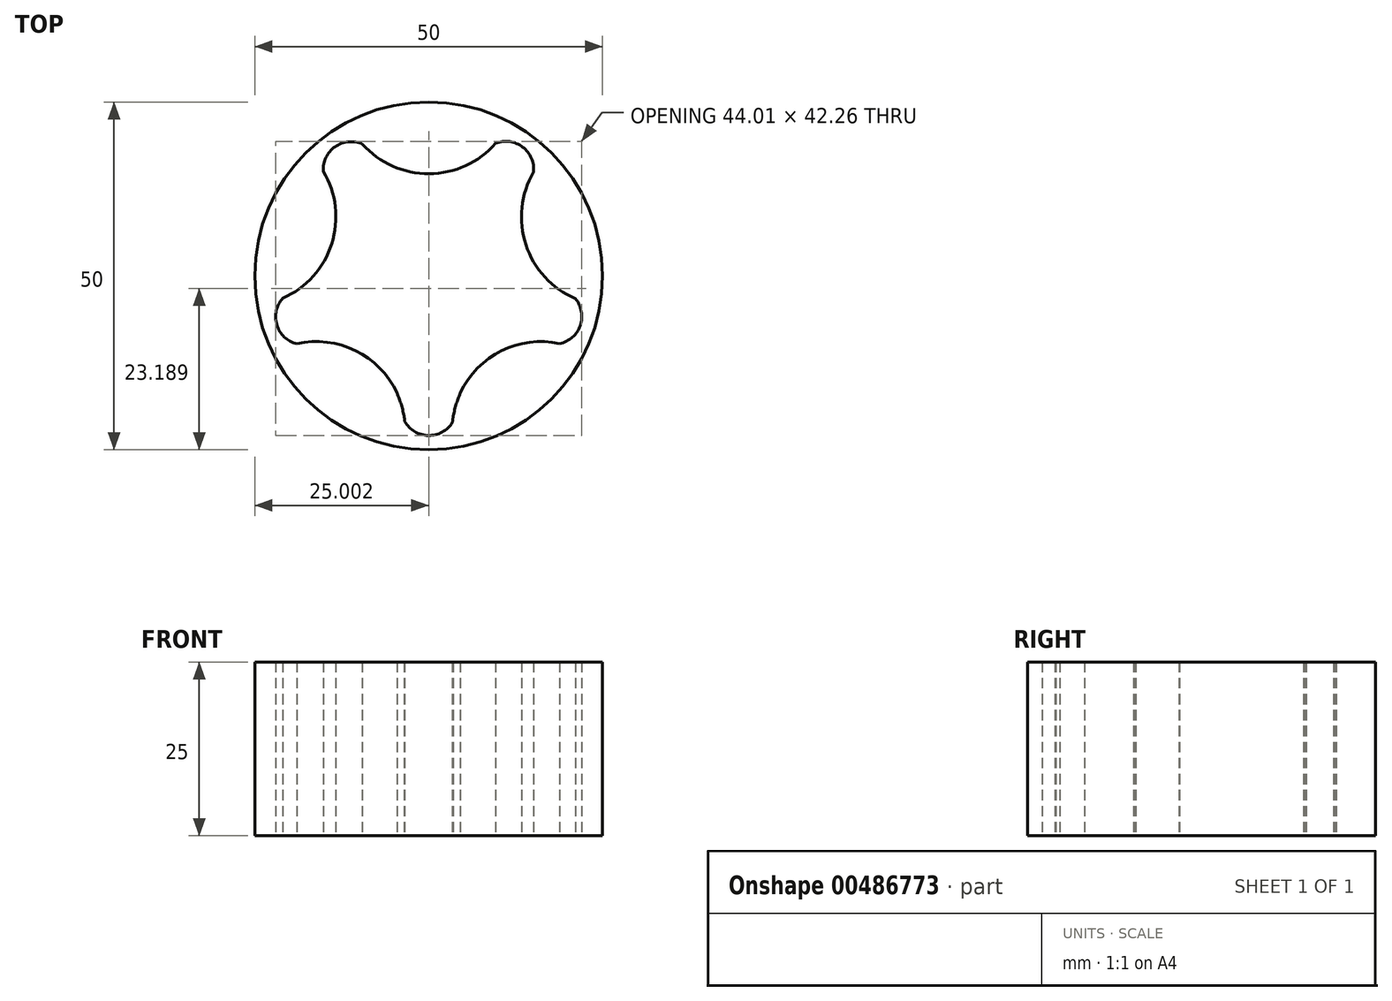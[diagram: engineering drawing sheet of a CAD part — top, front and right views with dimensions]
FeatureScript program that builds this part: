
annotation { "Feature Type Name" : "Feature", "Feature Type Description" : "" }
export const myFeature = defineFeature(function(context is Context, id is Id, definition is map)
    precondition{}
    {
        {
            var Q0;
            Q0=qCreatedBy(makeId("Top.planeOp"),FACE);
            var sketch = newSketch(context, id + "F0", { "sketchPlane" : qUnion([Q0])});
            skPoint(sketch, "E0", {"position": v(-17.88, 27.25) * mm});
            skPoint(sketch, "E1", {"position": v(-1.38, 10.75) * mm});
            skArc(sketch, "E2", {"start": v(-14.38, 27.25) * mm, "mid": v(-9.94, 18.7) * mm, "end": v(-1.38, 14.25) * mm});
            skArc(sketch, "E3.MirrorCS", {"start": v(-14.38, -5.75) * mm, "mid": v(-9.94, 2.8) * mm, "end": v(-1.38, 7.25) * mm});
            skArc(sketch, "E4.MirrorCS", {"start": v(-21.38, 27.25) * mm, "mid": v(-25.83, 18.7) * mm, "end": v(-34.38, 14.25) * mm});
            skArc(sketch, "E5.MirrorCS", {"start": v(-21.38, -5.75) * mm, "mid": v(-25.83, 2.8) * mm, "end": v(-34.38, 7.25) * mm});
            skArc(sketch, "E6", {"start": v(-14.38, 27.25) * mm, "mid": v(-17.88, 29.32) * mm, "end": v(-21.38, 27.25) * mm});
            skArc(sketch, "E7.MirrorCS", {"start": v(-14.38, -5.75) * mm, "mid": v(-17.88, -7.81) * mm, "end": v(-21.38, -5.75) * mm});
            skArc(sketch, "E8", {"start": v(-1.38, 7.25) * mm, "mid": v(0.68, 10.75) * mm, "end": v(-1.38, 14.25) * mm});
            skArc(sketch, "E9.MirrorCS", {"start": v(-34.38, 7.25) * mm, "mid": v(-36.45, 10.75) * mm, "end": v(-34.38, 14.25) * mm});
            skArc(sketch, "E10", {"start": v(-27.41, 33.59) * mm, "mid": v(-17.82, 29.32) * mm, "end": v(-8.26, 33.7) * mm});
            skArc(sketch, "E11.1.0", {"start": v(-38.86, 11.43) * mm, "mid": v(-31.83, 19.23) * mm, "end": v(-33.04, 29.67) * mm});
            skArc(sketch, "E11.2.0", {"start": v(-21.32, -6.3) * mm, "mid": v(-26.57, 2.8) * mm, "end": v(-36.87, 4.87) * mm});
            skArc(sketch, "E11.3.0", {"start": v(0.97, 4.9) * mm, "mid": v(-9.3, 2.71) * mm, "end": v(-14.46, -6.44) * mm});
            skArc(sketch, "E11.4.0", {"start": v(-2.8, 29.55) * mm, "mid": v(-3.9, 19.1) * mm, "end": v(3.22, 11.37) * mm});
            skPoint(sketch, "E11.center", {"position": v(-17.88, 14.63) * mm});
            skArc(sketch, "E12", {"start": v(-21.32, -6.3) * mm, "mid": v(-17.93, -8.3) * mm, "end": v(-14.46, -6.44) * mm});
            skArc(sketch, "E13.1.0", {"start": v(-38.86, 11.43) * mm, "mid": v(-39.72, 7.59) * mm, "end": v(-36.87, 4.87) * mm});
            skArc(sketch, "E13.2.0", {"start": v(-27.41, 33.59) * mm, "mid": v(-31.33, 33.22) * mm, "end": v(-33.04, 29.67) * mm});
            skArc(sketch, "E13.3.0", {"start": v(-2.8, 29.55) * mm, "mid": v(-4.36, 33.17) * mm, "end": v(-8.26, 33.7) * mm});
            skArc(sketch, "E13.4.0", {"start": v(0.97, 4.9) * mm, "mid": v(3.92, 7.5) * mm, "end": v(3.22, 11.37) * mm});
            skLineSegment(sketch, "E13.anchor1", {"start": v(-17.88, 14.63) * mm, "end": v(-21.32, -6.3) * mm, "construction": true});
            skLineSegment(sketch, "E13.anchor2", {"start": v(-17.88, 14.63) * mm, "end": v(0.97, 4.9) * mm, "construction": true});
            skCircle(sketch, "E14", {"center": v(-17.88, 14.63) * mm, "radius": 25 * mm});
            skLineSegment(sketch, "E15", {"start": v(-32.45, 10.75) * mm, "end": v(-3.32, 10.75) * mm});
            skLineSegment(sketch, "E16", {"start": v(-17.88, 25.32) * mm, "end": v(-17.88, -3.81) * mm});
            skPoint(sketch, "E17", {"position": v(-17.88, 10.75) * mm});
            skSolve(sketch);
        }
        {
            var Q0;
            Q0=makeQuery(id+"F0.imprint","IMPRINT",FACE,{"disambiguationData":[TD([[makeQuery(id+"F0.imprint","IMPRINT",EDGE,{"derivedFrom":sQuery(id+"F0.wireOp",EDGE,"E11.1.0")}),1.0]])]});
            extrude(context, id + "F1", {"entities" : qUnion([Q0]), "depth" : 25 * mm});
        }
    });
